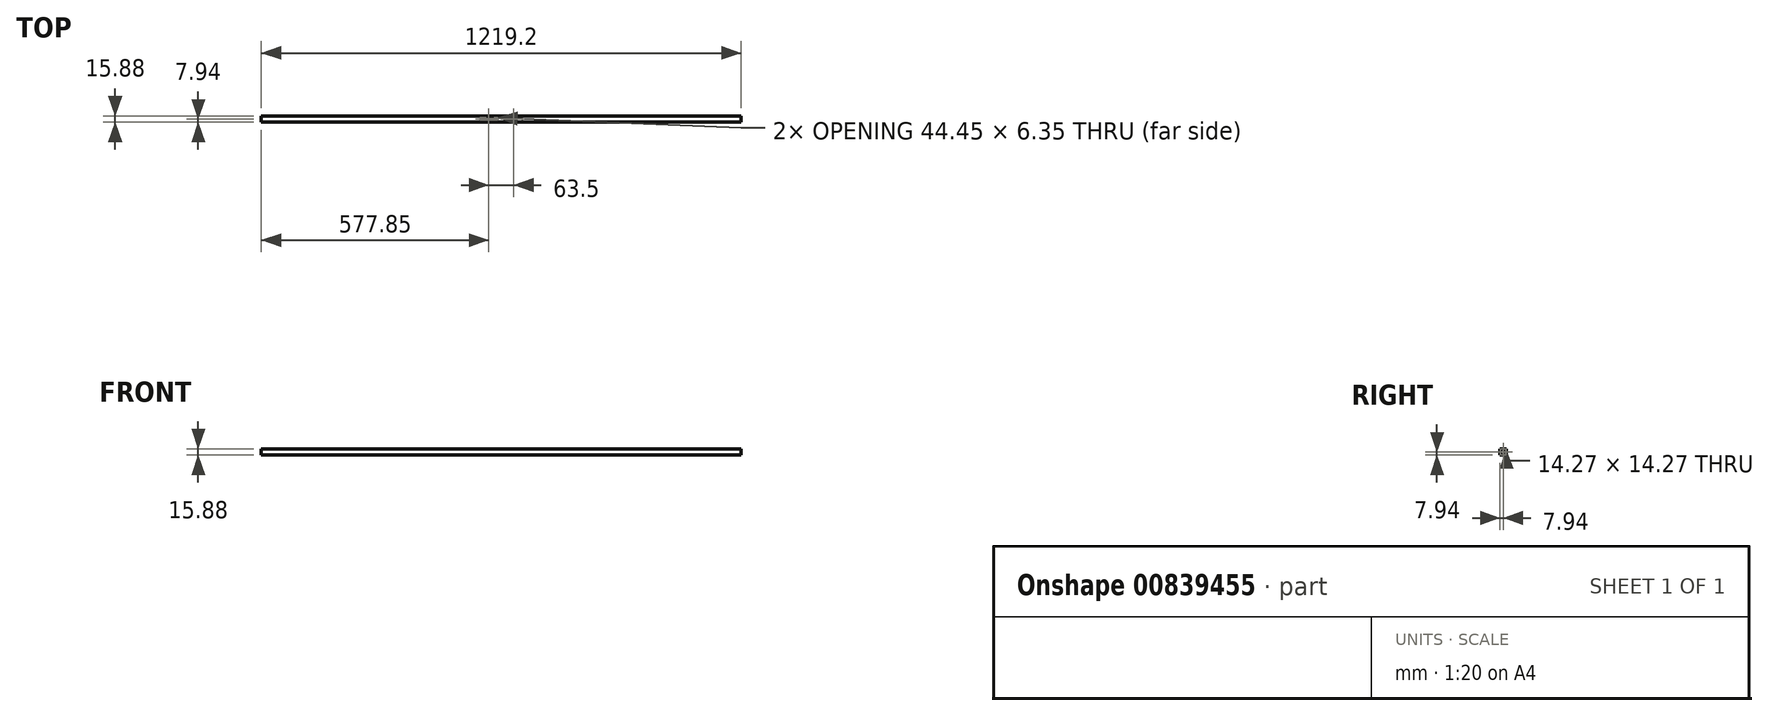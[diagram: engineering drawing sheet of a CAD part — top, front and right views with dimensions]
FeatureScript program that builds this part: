
annotation { "Feature Type Name" : "Feature", "Feature Type Description" : "" }
export const myFeature = defineFeature(function(context is Context, id is Id, definition is map)
    precondition{}
    {
        {
            var Q0;
            Q0=qCreatedBy(makeId("Right.planeOp"),FACE);
            var sketch = newSketch(context, id + "F0", { "sketchPlane" : qUnion([Q0])});
            skLineSegment(sketch, "E0.bottom", {"start": v(-7.94, -7.94) * mm, "end": v(7.94, -7.94) * mm});
            skLineSegment(sketch, "E0.top", {"start": v(-7.94, 7.94) * mm, "end": v(7.94, 7.94) * mm});
            skLineSegment(sketch, "E0.left", {"start": v(-7.94, -7.94) * mm, "end": v(-7.94, 7.94) * mm});
            skLineSegment(sketch, "E0.right", {"start": v(7.94, -7.94) * mm, "end": v(7.94, 7.94) * mm});
            skPoint(sketch, "E0.middle", {"position": v(0, 0) * mm});
            skLineSegment(sketch, "E1.bottom", {"start": v(-7.14, -7.14) * mm, "end": v(7.14, -7.14) * mm});
            skLineSegment(sketch, "E1.top", {"start": v(-7.14, 7.14) * mm, "end": v(7.14, 7.14) * mm});
            skLineSegment(sketch, "E1.left", {"start": v(-7.14, -7.14) * mm, "end": v(-7.14, 7.14) * mm});
            skLineSegment(sketch, "E1.right", {"start": v(7.14, -7.14) * mm, "end": v(7.14, 7.14) * mm});
            skSolve(sketch);
        }
        {
            var Q0;
            Q0=qSketchRegion(id+"F0",true);
            extrude(context, id + "F1", {"entities" : qUnion([Q0]), "depth" : 1219.2 * mm, "offsetDistance" : 25.4 * mm, "symmetric" : true});
        }
        {
            var Q0;
            Q0=makeQuery(id+"F1.opExtrude","SWEPT_FACE",FACE,{"disambiguationData":[OSD([sQuery(id+"F0.wireOp",EDGE,"E0.bottom")])]});
            var sketch = newSketch(context, id + "F2", { "sketchPlane" : qUnion([Q0])});
            skLineSegment(sketch, "E2", {"start": v(0, 0) * mm, "end": v(-31.75, 0) * mm, "construction": true});
            skLineSegment(sketch, "E3.bottom", {"start": v(-51.44, -3.17) * mm, "end": v(-12.06, -3.17) * mm});
            skLineSegment(sketch, "E3.top", {"start": v(-51.44, 3.18) * mm, "end": v(-12.06, 3.18) * mm});
            skLineSegment(sketch, "E3.left", {"start": v(-53.98, -0.63) * mm, "end": v(-53.98, 0.64) * mm});
            skLineSegment(sketch, "E3.right", {"start": v(-9.52, -0.63) * mm, "end": v(-9.52, 0.64) * mm});
            skPoint(sketch, "E3.middle", {"position": v(-31.75, 0) * mm});
            skPoint(sketch, "E4.visualSharp", {"position": v(-53.98, 3.18) * mm});
            skArc(sketch, "E4.filletArc", {"start": v(-51.44, 3.18) * mm, "mid": v(-53.23, 2.43) * mm, "end": v(-53.98, 0.64) * mm});
            skPoint(sketch, "E5.visualSharp", {"position": v(-53.98, -3.17) * mm});
            skArc(sketch, "E5.filletArc", {"start": v(-53.98, -0.63) * mm, "mid": v(-53.23, -2.43) * mm, "end": v(-51.44, -3.17) * mm});
            skPoint(sketch, "E6.visualSharp", {"position": v(-9.52, -3.17) * mm});
            skArc(sketch, "E6.filletArc", {"start": v(-12.06, -3.17) * mm, "mid": v(-10.27, -2.43) * mm, "end": v(-9.52, -0.63) * mm});
            skPoint(sketch, "E7.visualSharp", {"position": v(-9.52, 3.18) * mm});
            skArc(sketch, "E7.filletArc", {"start": v(-9.52, 0.64) * mm, "mid": v(-10.27, 2.43) * mm, "end": v(-12.06, 3.18) * mm});
            skLineSegment(sketch, "E8.MirrorCS", {"start": v(51.44, 3.18) * mm, "end": v(12.06, 3.18) * mm});
            skArc(sketch, "E9.MirrorCS", {"start": v(9.52, 0.64) * mm, "mid": v(10.27, 2.43) * mm, "end": v(12.06, 3.18) * mm});
            skArc(sketch, "E10.MirrorCS", {"start": v(12.06, -3.17) * mm, "mid": v(10.27, -2.43) * mm, "end": v(9.52, -0.63) * mm});
            skLineSegment(sketch, "E11.MirrorCS", {"start": v(51.44, -3.17) * mm, "end": v(12.06, -3.17) * mm});
            skArc(sketch, "E12.MirrorCS", {"start": v(53.98, -0.63) * mm, "mid": v(53.23, -2.43) * mm, "end": v(51.44, -3.17) * mm});
            skArc(sketch, "E13.MirrorCS", {"start": v(51.44, 3.18) * mm, "mid": v(53.23, 2.43) * mm, "end": v(53.98, 0.64) * mm});
            skLineSegment(sketch, "E14.MirrorCS", {"start": v(53.98, -0.63) * mm, "end": v(53.98, 0.64) * mm});
            skLineSegment(sketch, "E15.MirrorCS", {"start": v(9.52, -0.63) * mm, "end": v(9.52, 0.64) * mm});
            skSolve(sketch);
        }
        {
            var Q0;
            Q0=qSketchRegion(id+"F2",true);
            extrude(context, id + "F3", {"entities" : qUnion([Q0]), "operationType" : NewBodyOperationType.REMOVE, "oppositeDirection" : true, "depth" : 5.08 * mm, "offsetDistance" : 25.4 * mm});
        }
    });
